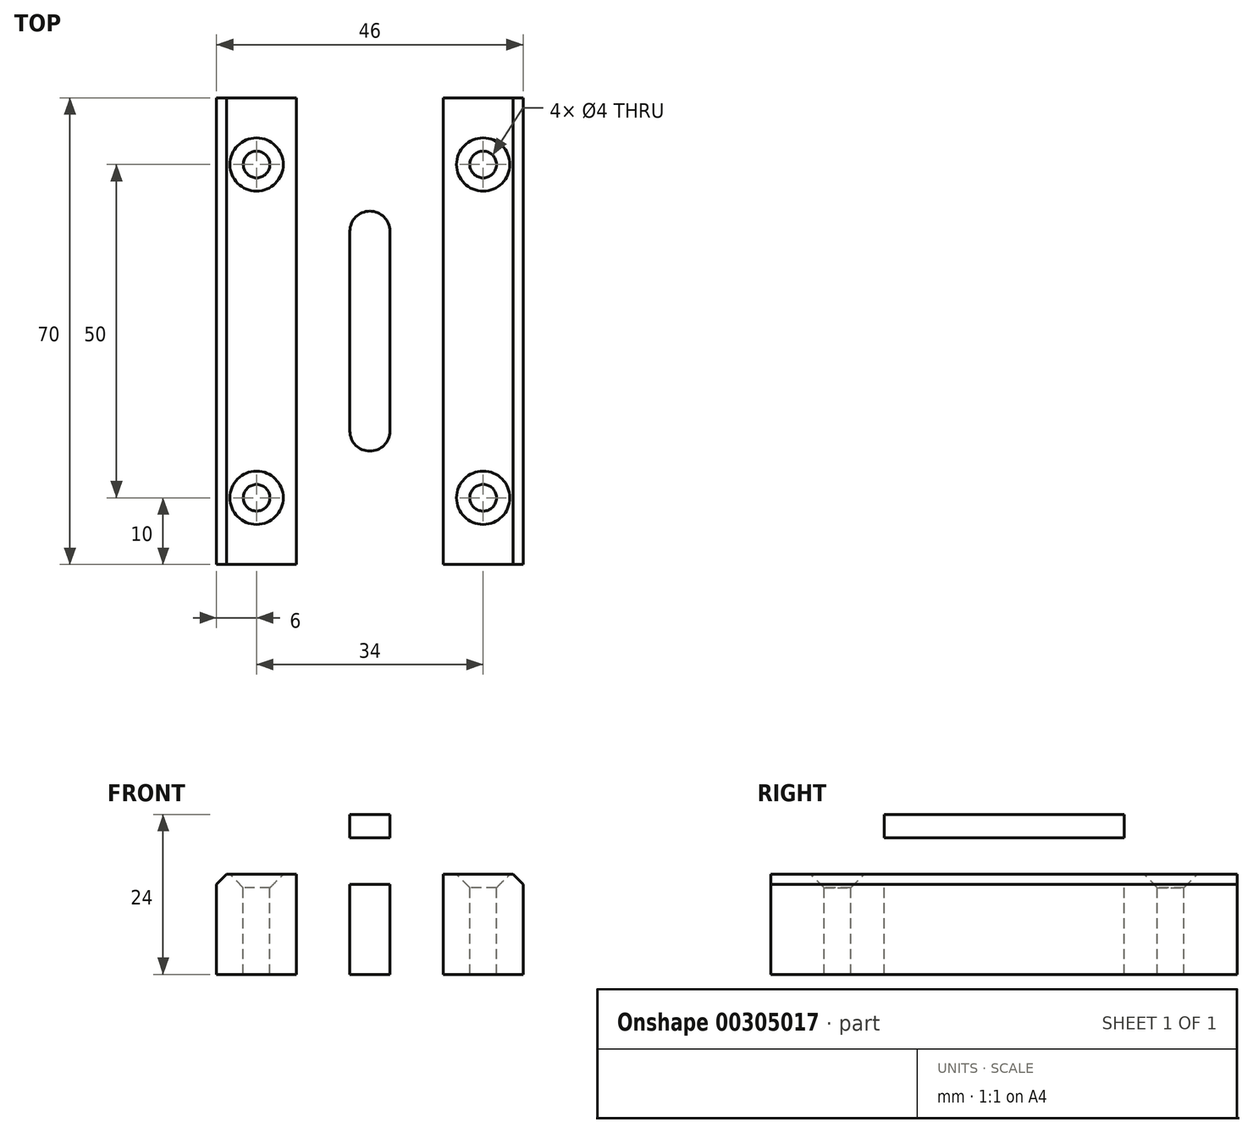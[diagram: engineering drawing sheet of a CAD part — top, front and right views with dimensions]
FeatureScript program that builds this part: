
annotation { "Feature Type Name" : "Feature", "Feature Type Description" : "" }
export const myFeature = defineFeature(function(context is Context, id is Id, definition is map)
    precondition{}
    {
        {
            var Q0;
            Q0=qCreatedBy(makeId("Front.planeOp"),FACE);
            var sketch = newSketch(context, id + "F0", { "sketchPlane" : qUnion([Q0])});
            skLineSegment(sketch, "E0", {"start": v(-23, 0) * mm, "end": v(23, 0) * mm});
            skLineSegment(sketch, "E1", {"start": v(23, 0) * mm, "end": v(23, 15) * mm});
            skLineSegment(sketch, "E2", {"start": v(23, 15) * mm, "end": v(11, 15) * mm});
            skLineSegment(sketch, "E3", {"start": v(11, 15) * mm, "end": v(11, 24) * mm});
            skLineSegment(sketch, "E4", {"start": v(11, 24) * mm, "end": v(-11, 24) * mm});
            skLineSegment(sketch, "E5", {"start": v(-11, 24) * mm, "end": v(-11, 15) * mm});
            skLineSegment(sketch, "E6", {"start": v(-11, 15) * mm, "end": v(-23, 15) * mm});
            skLineSegment(sketch, "E7", {"start": v(-23, 15) * mm, "end": v(-23, 0) * mm});
            skPoint(sketch, "E8", {"position": v(0, 0) * mm});
            skLineSegment(sketch, "E9.bottom", {"start": v(7.5, 20.5) * mm, "end": v(-7.5, 20.5) * mm});
            skLineSegment(sketch, "E9.top", {"start": v(7.5, 13.5) * mm, "end": v(-7.5, 13.5) * mm});
            skLineSegment(sketch, "E9.left", {"start": v(7.5, 20.5) * mm, "end": v(7.5, 13.5) * mm});
            skLineSegment(sketch, "E9.right", {"start": v(-7.5, 20.5) * mm, "end": v(-7.5, 13.5) * mm});
            skPoint(sketch, "E9.middle", {"position": v(0, 17) * mm});
            skSolve(sketch);
        }
        {
            var Q0;
            Q0=makeQuery(id+"F0.imprint","IMPRINT",FACE,{"disambiguationData":[TD([[makeQuery(id+"F0.imprint","IMPRINT",EDGE,{"derivedFrom":sQuery(id+"F0.wireOp",EDGE,"E0")}),1.0]])]});
            extrude(context, id + "F1", {"entities" : qUnion([Q0]), "endBound" : BoundingType.SYMMETRIC, "depth" : 70 * mm});
        }
        {
            var Q0;
            Q0=makeQuery(id+"F1.opExtrude","SWEPT_FACE",FACE,{"disambiguationData":[OSD([sQuery(id+"F0.wireOp",EDGE,"E4")])]});
            var sketch = newSketch(context, id + "F2", { "sketchPlane" : qUnion([Q0])});
            skLineSegment(sketch, "E10", {"start": v(0, 15) * mm, "end": v(0, -15) * mm});
            skArc(sketch, "E11.0.startCap", {"start": v(-3, 15) * mm, "mid": v(0, 18) * mm, "end": v(3, 15) * mm});
            skArc(sketch, "E11.0.endCap", {"start": v(3, -15) * mm, "mid": v(0, -18) * mm, "end": v(-3, -15) * mm});
            skLineSegment(sketch, "E11.0.left", {"start": v(3, 15) * mm, "end": v(3, -15) * mm});
            skLineSegment(sketch, "E11.0.right", {"start": v(-3, 15) * mm, "end": v(-3, -15) * mm});
            skPoint(sketch, "E12", {"position": v(0, 0) * mm});
            skSolve(sketch);
        }
        {
            var Q0;
            Q0=makeQuery(id+"F2.imprint","IMPRINT",FACE,{"disambiguationData":[TD([[makeQuery(id+"F2.imprint","IMPRINT",EDGE,{"derivedFrom":sQuery(id+"F2.wireOp",EDGE,"E11.0.startCap")}),-1.0]])]});
            extrude(context, id + "F3", {"entities" : qUnion([Q0]), "operationType" : NewBodyOperationType.REMOVE, "endBound" : BoundingType.UP_TO_NEXT, "oppositeDirection" : true, "depth" : 25 * mm});
        }
        {
            var Q0;
            Q0=makeQuery(id+"F1.opExtrude","SWEPT_EDGE",EDGE,{"disambiguationData":[OSD([sQuery(id+"F0.wireOp",EDGE,"E5"),sQuery(id+"F0.wireOp",EDGE,"E6")])]});
            var Q1;
            Q1=makeQuery(id+"F1.opExtrude","SWEPT_EDGE",EDGE,{"disambiguationData":[OSD([sQuery(id+"F0.wireOp",EDGE,"E3"),sQuery(id+"F0.wireOp",EDGE,"E4")])]});
            var Q2;
            Q2=makeQuery(id+"F1.opExtrude","SWEPT_EDGE",EDGE,{"disambiguationData":[OSD([sQuery(id+"F0.wireOp",EDGE,"E4"),sQuery(id+"F0.wireOp",EDGE,"E5")])]});
            var Q3;
            Q3=makeQuery(id+"F1.opExtrude","SWEPT_EDGE",EDGE,{"disambiguationData":[OSD([sQuery(id+"F0.wireOp",EDGE,"E2"),sQuery(id+"F0.wireOp",EDGE,"E3")])]});
            var Q4;
            Q4=makeQuery(id+"F1.opExtrude","SWEPT_EDGE",EDGE,{"disambiguationData":[OSD([sQuery(id+"F0.wireOp",EDGE,"E6"),sQuery(id+"F0.wireOp",EDGE,"E7")])]});
            var Q5;
            Q5=makeQuery(id+"F1.opExtrude","SWEPT_EDGE",EDGE,{"disambiguationData":[OSD([sQuery(id+"F0.wireOp",EDGE,"E1"),sQuery(id+"F0.wireOp",EDGE,"E2")])]});
            chamfer(context, id + "F4", {"entities" : qUnion([Q0, Q1, Q2, Q3, Q4, Q5]), "width" : 1.5 * mm, "tangentPropagation" : true});
        }
        {
            var Q0;
            Q0=makeQuery(id+"F1.opExtrude","SWEPT_FACE",FACE,{"disambiguationData":[OSD([sQuery(id+"F0.wireOp",EDGE,"E6")])]});
            var sketch = newSketch(context, id + "F5", { "sketchPlane" : qUnion([Q0])});
            skPoint(sketch, "E13", {"position": v(-17, -25) * mm});
            skPoint(sketch, "E14", {"position": v(-17, 25) * mm});
            skPoint(sketch, "E15", {"position": v(17, 25) * mm});
            skPoint(sketch, "E16", {"position": v(17, -25) * mm});
            skPoint(sketch, "E17", {"position": v(-17, 35) * mm});
            skLineSegment(sketch, "E18", {"start": v(-17, 25) * mm, "end": v(0, 25) * mm, "construction": true});
            skLineSegment(sketch, "E19", {"start": v(0, 25) * mm, "end": v(17, 25) * mm, "construction": true});
            skSolve(sketch);
        }
        {
            var Q0;
            Q0=sQuery(id+"F5.wireOp",VERTEX,"E15");
            var Q1;
            Q1=sQuery(id+"F5.wireOp",VERTEX,"E16");
            var Q2;
            Q2=sQuery(id+"F5.wireOp",VERTEX,"E13");
            var Q3;
            Q3=sQuery(id+"F5.wireOp",VERTEX,"E14");
            var Q4;
            Q4=makeQuery(id+"F1.opExtrude","SWEPT_BODY",BODY,{"disambiguationData":[OSD([sQuery(id+"F0.wireOp",EDGE,"E0"),sQuery(id+"F0.wireOp",EDGE,"E1"),sQuery(id+"F0.wireOp",EDGE,"E2"),sQuery(id+"F0.wireOp",EDGE,"E3"),sQuery(id+"F0.wireOp",EDGE,"E4"),sQuery(id+"F0.wireOp",EDGE,"E5"),sQuery(id+"F0.wireOp",EDGE,"E6"),sQuery(id+"F0.wireOp",EDGE,"E7"),sQuery(id+"F0.wireOp",EDGE,"E9.bottom"),sQuery(id+"F0.wireOp",EDGE,"E9.top"),sQuery(id+"F0.wireOp",EDGE,"E9.left"),sQuery(id+"F0.wireOp",EDGE,"E9.right")])]});
            hole(context, id + "F6", {"style" : HoleStyle.C_SINK, "endStyle" : HoleEndStyle.THROUGH, "holeDiameter" : 4 * mm, "cSinkDiameter" : 8 * mm, "cSinkAngle" : 90 * degree, "tappedDepth" : 12 * mm, "tapClearance" : 3, "locations" : qUnion([Q0, Q1, Q2, Q3]), "scope" : qUnion([Q4])});
        }
    });
